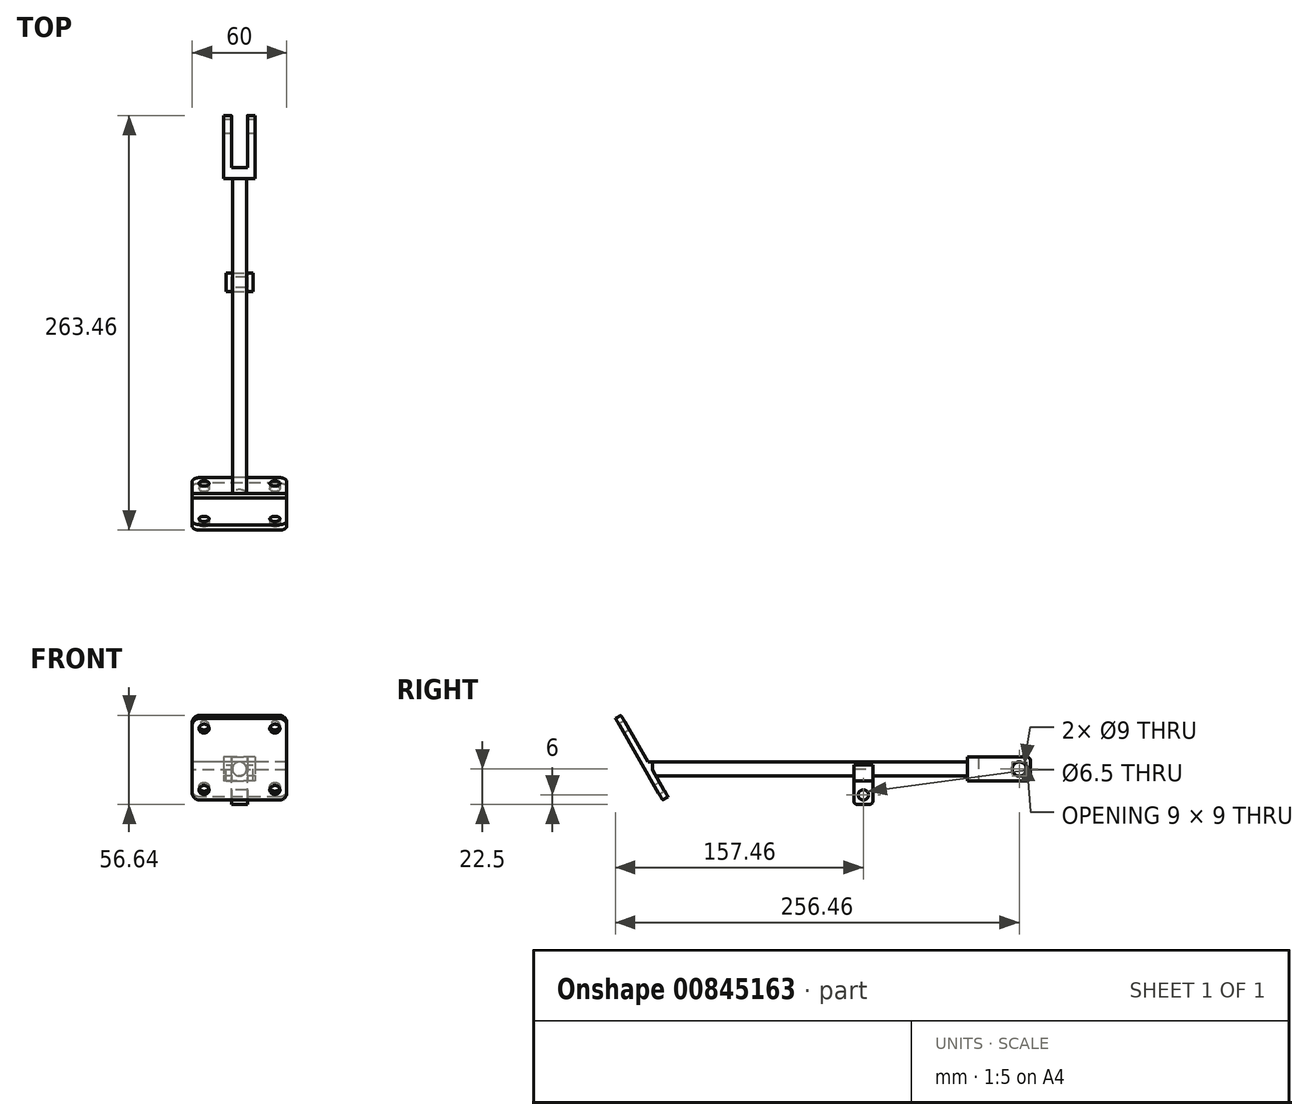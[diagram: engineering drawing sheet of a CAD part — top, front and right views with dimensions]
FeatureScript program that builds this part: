
annotation { "Feature Type Name" : "Feature", "Feature Type Description" : "" }
export const myFeature = defineFeature(function(context is Context, id is Id, definition is map)
    precondition{}
    {
        {
            var Q0;
            Q0=qCreatedBy(makeId("Top.planeOp"),FACE);
            var sketch = newSketch(context, id + "F0", { "sketchPlane" : qUnion([Q0])});
            skLineSegment(sketch, "E0.bottom", {"start": v(10, -20) * mm, "end": v(-10, -20) * mm});
            skLineSegment(sketch, "E0.top", {"start": v(10, 20) * mm, "end": v(5, 20) * mm});
            skLineSegment(sketch, "E0.left", {"start": v(10, -20) * mm, "end": v(10, 20) * mm});
            skLineSegment(sketch, "E0.right", {"start": v(-10, -20) * mm, "end": v(-10, 20) * mm});
            skPoint(sketch, "E0.middle", {"position": v(0, 0) * mm});
            skLineSegment(sketch, "E1.top", {"start": v(-5, -13) * mm, "end": v(5, -13) * mm});
            skLineSegment(sketch, "E1.left", {"start": v(-5, 20) * mm, "end": v(-5, -13) * mm});
            skLineSegment(sketch, "E1.right", {"start": v(5, 20) * mm, "end": v(5, -13) * mm});
            skLineSegment(sketch, "E2.trimOffspring", {"start": v(-5, 20) * mm, "end": v(-10, 20) * mm});
            skSolve(sketch);
        }
        {
            var Q0;
            Q0 = qSketchRegion(id + "F0", true);
            extrude(context, id + "F1", {"entities" : qUnion([Q0]), "depth" : 15 * mm, "offsetDistance" : 25 * mm});
        }
        {
            var Q0;
            Q0=makeQuery(id+"F1.opExtrude","SWEPT_FACE",FACE,{"disambiguationData":[OSD([sQuery(id+"F0.wireOp",EDGE,"E0.bottom")])]});
            var sketch = newSketch(context, id + "F2", { "sketchPlane" : qUnion([Q0])});
            skCircle(sketch, "E3", {"center": v(0, 7.5) * mm, "radius": 4.5 * mm});
            skLineSegment(sketch, "E4", {"start": v(0, 15) * mm, "end": v(0, 0) * mm, "construction": true});
            skLineSegment(sketch, "E5", {"start": v(0, 0) * mm, "end": v(0, 7.5) * mm});
            skLineSegment(sketch, "E6", {"start": v(0, 7.5) * mm, "end": v(0.95, 7.5) * mm, "construction": true});
            skSolve(sketch);
        }
        {
            var Q0;
            Q0 = qSketchRegion(id + "F2", true);
            extrude(context, id + "F3", {"entities" : qUnion([Q0]), "operationType" : NewBodyOperationType.ADD, "depth" : 200 * mm, "offsetDistance" : 25 * mm});
        }
        {
            var Q0;
            Q0=makeQuery(id+"F1.opExtrude","SWEPT_FACE",FACE,{"disambiguationData":[OSD([sQuery(id+"F0.wireOp",EDGE,"E0.right")])]});
            var sketch = newSketch(context, id + "F4", { "sketchPlane" : qUnion([Q0])});
            skLineSegment(sketch, "E7", {"start": v(-20, 7.5) * mm, "end": v(-13, 7.5) * mm, "construction": true});
            skCircle(sketch, "E8", {"center": v(-13, 7.5) * mm, "radius": 4.5 * mm});
            skSolve(sketch);
        }
        {
            var Q0;
            Q0 = qSketchRegion(id + "F4", true);
            extrude(context, id + "F5", {"entities" : qUnion([Q0]), "operationType" : NewBodyOperationType.REMOVE, "oppositeDirection" : true, "depth" : 25 * mm, "offsetDistance" : 25 * mm});
        }
        {
            var Q0;
            Q0=makeQuery(id+"F1.opExtrude","CAP_EDGE",EDGE,{"disambiguationData":[OSD([sQuery(id+"F0.wireOp",EDGE,"E2.trimOffspring")])],"isStart":false});
            var Q1;
            Q1=makeQuery(id+"F1.opExtrude","CAP_EDGE",EDGE,{"disambiguationData":[OSD([sQuery(id+"F0.wireOp",EDGE,"E0.top")])],"isStart":false});
            var Q2;
            Q2=makeQuery(id+"F1.opExtrude","CAP_EDGE",EDGE,{"disambiguationData":[OSD([sQuery(id+"F0.wireOp",EDGE,"E0.top")])],"isStart":true});
            var Q3;
            Q3=makeQuery(id+"F1.opExtrude","CAP_EDGE",EDGE,{"disambiguationData":[OSD([sQuery(id+"F0.wireOp",EDGE,"E2.trimOffspring")])],"isStart":true});
            fillet(context, id + "F6", {"entities" : qUnion([Q0, Q1, Q2, Q3]), "radius" : 2 * mm, "tangentPropagation" : true, "allowEdgeOverflow" : false});
        }
        {
            var Q0;
            Q0=qCreatedBy(makeId("Right.planeOp"),FACE);
            var sketch = newSketch(context, id + "F7", { "sketchPlane" : qUnion([Q0])});
            skLineSegment(sketch, "E9", {"start": v(-220, 7) * mm, "end": v(-240, 41.64) * mm});
            skLineSegment(sketch, "E10", {"start": v(-220, 7) * mm, "end": v(-220, 30.25) * mm, "construction": true});
            skLineSegment(sketch, "E11", {"start": v(-220, 7) * mm, "end": v(-210, -10.32) * mm});
            skLineSegment(sketch, "E12", {"start": v(-210, -10.32) * mm, "end": v(-213.46, -12.32) * mm});
            skLineSegment(sketch, "E13", {"start": v(-213.46, -12.32) * mm, "end": v(-243.46, 39.64) * mm});
            skLineSegment(sketch, "E14", {"start": v(-243.46, 39.64) * mm, "end": v(-240, 41.64) * mm});
            skLineSegment(sketch, "E15", {"start": v(-20, 0) * mm, "end": v(-20, 7) * mm});
            skLineSegment(sketch, "E16", {"start": v(-20, 7) * mm, "end": v(-220, 7) * mm});
            skLineSegment(sketch, "E17", {"start": v(-220, 7) * mm, "end": v(-220, 12) * mm});
            skLineSegment(sketch, "E18", {"start": v(-220, 12) * mm, "end": v(-222.89, 12) * mm});
            skSolve(sketch);
        }
        {
            var Q0;
            Q0 = qSketchRegion(id + "F7", true);
            extrude(context, id + "F8", {"entities" : qUnion([Q0]), "operationType" : NewBodyOperationType.ADD, "depth" : 30 * mm, "offsetDistance" : 25 * mm, "hasSecondDirection" : true, "secondDirectionOppositeDirection" : true, "secondDirectionDepth" : 30 * mm});
        }
        {
            var Q0;
            Q0=makeQuery(id+"F8.opExtrude","SWEPT_FACE",FACE,{"disambiguationData":[OSD([sQuery(id+"F7.wireOp",EDGE,"E13")])]});
            var sketch = newSketch(context, id + "F9", { "sketchPlane" : qUnion([Q0])});
            skPoint(sketch, "E19.middle", {"position": v(-3.9, 78.7) * mm});
            skLineSegment(sketch, "E20", {"start": v(0, 156.06) * mm, "end": v(0, 96.06) * mm, "construction": true});
            skLineSegment(sketch, "E21", {"start": v(-30, 126.06) * mm, "end": v(30, 126.06) * mm, "construction": true});
            skLineSegment(sketch, "E22.bottom", {"start": v(22.5, 103.56) * mm, "end": v(-22.5, 103.56) * mm, "construction": true});
            skLineSegment(sketch, "E22.top", {"start": v(22.5, 148.56) * mm, "end": v(-22.5, 148.56) * mm, "construction": true});
            skLineSegment(sketch, "E22.left", {"start": v(22.5, 103.56) * mm, "end": v(22.5, 148.56) * mm, "construction": true});
            skLineSegment(sketch, "E22.right", {"start": v(-22.5, 103.56) * mm, "end": v(-22.5, 148.56) * mm, "construction": true});
            skPoint(sketch, "E22.middle", {"position": v(0, 126.06) * mm});
            skCircle(sketch, "E23", {"center": v(-22.5, 148.56) * mm, "radius": 3.25 * mm});
            skCircle(sketch, "E24", {"center": v(22.5, 148.56) * mm, "radius": 3.25 * mm});
            skCircle(sketch, "E25", {"center": v(-22.5, 103.56) * mm, "radius": 3.25 * mm});
            skCircle(sketch, "E26", {"center": v(22.5, 103.56) * mm, "radius": 3.25 * mm});
            skSolve(sketch);
        }
        {
            var Q0;
            Q0 = qSketchRegion(id + "F9", true);
            extrude(context, id + "F10", {"entities" : qUnion([Q0]), "operationType" : NewBodyOperationType.REMOVE, "oppositeDirection" : true, "depth" : 25 * mm, "offsetDistance" : 25 * mm});
        }
        {
            var Q0;
            Q0=qCreatedBy(makeId("Front.planeOp"),FACE);
            cPlane(context, id + "F11", {"entities" : qUnion([Q0]), "cplaneType" : CPlaneType.OFFSET, "offset" : 80 * mm, "width" : 150 * mm, "height" : 150 * mm});
        }
        {
            var Q0;
            Q0=qCreatedBy(id+"F11.planeOp",FACE);
            var sketch = newSketch(context, id + "F12", { "sketchPlane" : qUnion([Q0])});
            skLineSegment(sketch, "E27.bottom", {"start": v(-5, -15) * mm, "end": v(5, -15) * mm});
            skLineSegment(sketch, "E27.top", {"start": v(-8.5, 10) * mm, "end": v(-4.5, 10) * mm});
            skLineSegment(sketch, "E27.left", {"start": v(-8.5, 0) * mm, "end": v(-8.5, 10) * mm});
            skLineSegment(sketch, "E27.right", {"start": v(8.5, 0) * mm, "end": v(8.5, 10) * mm});
            skLineSegment(sketch, "E28.left", {"start": v(4.5, 10) * mm, "end": v(4.5, 7.5) * mm});
            skLineSegment(sketch, "E28.right", {"start": v(-4.5, 10) * mm, "end": v(-4.5, 7.5) * mm});
            skLineSegment(sketch, "E29.trimOffspring", {"start": v(4.5, 10) * mm, "end": v(8.5, 10) * mm});
            skLineSegment(sketch, "E30", {"start": v(0, 3) * mm, "end": v(0, 7.5) * mm, "construction": true});
            skArc(sketch, "E31", {"start": v(-4.5, 7.5) * mm, "mid": v(0, 3) * mm, "end": v(4.5, 7.5) * mm});
            skLineSegment(sketch, "E32.top", {"start": v(8.5, 0) * mm, "end": v(5, 0) * mm});
            skLineSegment(sketch, "E32.right", {"start": v(5, -15) * mm, "end": v(5, 0) * mm});
            skLineSegment(sketch, "E33.top", {"start": v(-8.5, 0) * mm, "end": v(-5, 0) * mm});
            skLineSegment(sketch, "E33.right", {"start": v(-5, -15) * mm, "end": v(-5, 0) * mm});
            skSolve(sketch);
        }
        {
            var Q0;
            Q0 = qSketchRegion(id + "F12", true);
            extrude(context, id + "F13", {"entities" : qUnion([Q0]), "operationType" : NewBodyOperationType.ADD, "depth" : 12 * mm, "offsetDistance" : 25 * mm});
        }
        {
            var Q0;
            Q0=makeQuery(id+"F13.opExtrude","SWEPT_FACE",FACE,{"disambiguationData":[OSD([sQuery(id+"F12.wireOp",EDGE,"E33.right")])]});
            var sketch = newSketch(context, id + "F14", { "sketchPlane" : qUnion([Q0])});
            skCircle(sketch, "E34", {"center": v(86, -9) * mm, "radius": 3.25 * mm});
            skPoint(sketch, "E34.centerSnap0", {"position": v(86, -15) * mm});
            skPoint(sketch, "E34.centerSnap1", {"position": v(92, -9) * mm});
            skSolve(sketch);
        }
        {
            var Q0;
            Q0 = qSketchRegion(id + "F14", true);
            extrude(context, id + "F15", {"entities" : qUnion([Q0]), "operationType" : NewBodyOperationType.REMOVE, "oppositeDirection" : true, "depth" : 25 * mm, "offsetDistance" : 25 * mm});
        }
        {
            var Q0;
            Q0=makeQuery(id+"F13.opExtrude","CAP_EDGE",EDGE,{"disambiguationData":[OSD([sQuery(id+"F12.wireOp",EDGE,"E27.bottom")])],"isStart":true});
            var Q1;
            Q1=makeQuery(id+"F13.opExtrude","CAP_EDGE",EDGE,{"disambiguationData":[OSD([sQuery(id+"F12.wireOp",EDGE,"E27.bottom")])],"isStart":false});
            fillet(context, id + "F16", {"entities" : qUnion([Q0, Q1]), "radius" : 2 * mm, "tangentPropagation" : true, "allowEdgeOverflow" : false});
        }
        {
            var Q0;
            Q0=makeQuery(id+"F8.opExtrude","CAP_EDGE",EDGE,{"disambiguationData":[OSD([sQuery(id+"F7.wireOp",EDGE,"E14")])],"isStart":true});
            var Q1;
            Q1=makeQuery(id+"F8.opExtrude","CAP_EDGE",EDGE,{"disambiguationData":[OSD([sQuery(id+"F7.wireOp",EDGE,"E14")])],"isStart":false});
            var Q2;
            Q2=makeQuery(id+"F8.opExtrude","CAP_EDGE",EDGE,{"disambiguationData":[OSD([sQuery(id+"F7.wireOp",EDGE,"E12")])],"isStart":true});
            var Q3;
            Q3=makeQuery(id+"F8.opExtrude","CAP_EDGE",EDGE,{"disambiguationData":[OSD([sQuery(id+"F7.wireOp",EDGE,"E12")])],"isStart":false});
            fillet(context, id + "F17", {"entities" : qUnion([Q0, Q1, Q2, Q3]), "radius" : 5 * mm, "tangentPropagation" : true, "allowEdgeOverflow" : false});
        }
    });
